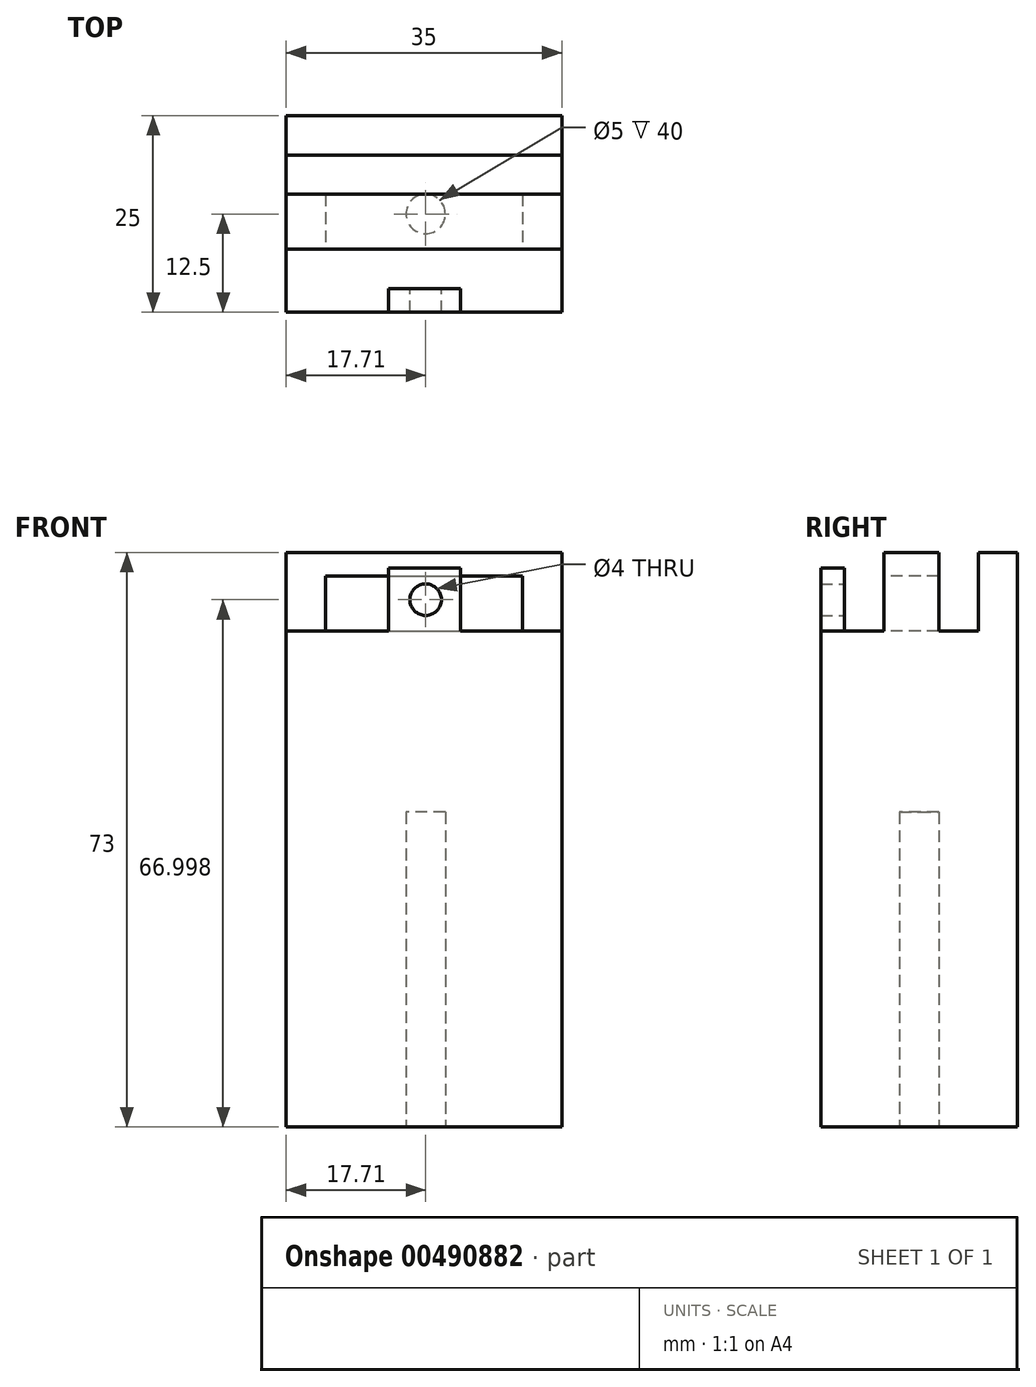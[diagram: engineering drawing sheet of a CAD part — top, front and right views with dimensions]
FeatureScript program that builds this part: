
annotation { "Feature Type Name" : "Feature", "Feature Type Description" : "" }
export const myFeature = defineFeature(function(context is Context, id is Id, definition is map)
    precondition{}
    {
        {
            var Q0;
            Q0=qCreatedBy(makeId("Top.planeOp"),FACE);
            var sketch = newSketch(context, id + "F0", { "sketchPlane" : qUnion([Q0])});
            skLineSegment(sketch, "E0.bottom", {"start": v(-17.7, 12.5) * mm, "end": v(17.3, 12.5) * mm});
            skLineSegment(sketch, "E0.top", {"start": v(-17.7, -12.5) * mm, "end": v(17.3, -12.5) * mm});
            skLineSegment(sketch, "E0.left", {"start": v(-17.7, 12.5) * mm, "end": v(-17.7, -12.5) * mm});
            skLineSegment(sketch, "E0.right", {"start": v(17.3, 12.5) * mm, "end": v(17.3, -12.5) * mm});
            skCircle(sketch, "E1", {"center": v(0, 0) * mm, "radius": 2.5 * mm});
            skSolve(sketch);
        }
        {
            var Q0;
            Q0 = qSketchRegion(id + "F0", true);
            extrude(context, id + "F1", {"entities" : qUnion([Q0]), "depth" : 40 * mm});
        }
        {
            var Q0;
            Q0=makeQuery(id+"F1.opExtrude","CAP_FACE",FACE,{"disambiguationData":[OSD([sQuery(id+"F0.wireOp",EDGE,"E0.bottom"),sQuery(id+"F0.wireOp",EDGE,"E0.top"),sQuery(id+"F0.wireOp",EDGE,"E0.left"),sQuery(id+"F0.wireOp",EDGE,"E0.right"),sQuery(id+"F0.wireOp",EDGE,"E1")])],"isStart":false});
            var sketch = newSketch(context, id + "F2", { "sketchPlane" : qUnion([Q0])});
            skLineSegment(sketch, "E2.bottom", {"start": v(-17.7, 12.5) * mm, "end": v(17.3, 12.5) * mm});
            skLineSegment(sketch, "E2.top", {"start": v(-17.7, -12.5) * mm, "end": v(17.3, -12.5) * mm});
            skLineSegment(sketch, "E2.left", {"start": v(-17.7, 12.5) * mm, "end": v(-17.7, -12.5) * mm});
            skLineSegment(sketch, "E2.right", {"start": v(17.3, 12.5) * mm, "end": v(17.3, -12.5) * mm});
            skSolve(sketch);
        }
        {
            var Q0;
            Q0 = qSketchRegion(id + "F2", true);
            extrude(context, id + "F3", {"entities" : qUnion([Q0]), "operationType" : NewBodyOperationType.ADD, "depth" : 23 * mm});
        }
        {
            var Q0;
            Q0=makeQuery(id+"F3.opExtrude","CAP_FACE",FACE,{"disambiguationData":[OSD([sQuery(id+"F2.wireOp",EDGE,"E2.bottom"),sQuery(id+"F2.wireOp",EDGE,"E2.top"),sQuery(id+"F2.wireOp",EDGE,"E2.left"),sQuery(id+"F2.wireOp",EDGE,"E2.right")])],"isStart":false});
            var sketch = newSketch(context, id + "F4", { "sketchPlane" : qUnion([Q0])});
            skLineSegment(sketch, "E3.bottom", {"start": v(-17.7, 12.5) * mm, "end": v(17.3, 12.5) * mm});
            skLineSegment(sketch, "E3.top", {"start": v(-17.7, 7.5) * mm, "end": v(17.3, 7.5) * mm});
            skLineSegment(sketch, "E3.left", {"start": v(-17.7, 12.5) * mm, "end": v(-17.7, 7.5) * mm});
            skLineSegment(sketch, "E3.right", {"start": v(17.3, 12.5) * mm, "end": v(17.3, 7.5) * mm});
            skSolve(sketch);
        }
        {
            var Q0;
            Q0 = qSketchRegion(id + "F4", true);
            extrude(context, id + "F5", {"entities" : qUnion([Q0]), "operationType" : NewBodyOperationType.ADD, "depth" : 10 * mm});
        }
        {
            var Q0;
            Q0=makeQuery(id+"F3.opExtrude","CAP_FACE",FACE,{"disambiguationData":[OSD([sQuery(id+"F2.wireOp",EDGE,"E2.bottom"),sQuery(id+"F2.wireOp",EDGE,"E2.top"),sQuery(id+"F2.wireOp",EDGE,"E2.left"),sQuery(id+"F2.wireOp",EDGE,"E2.right")])],"isStart":false});
            var sketch = newSketch(context, id + "F6", { "sketchPlane" : qUnion([Q0])});
            skLineSegment(sketch, "E4.bottom", {"start": v(-17.7, 2.5) * mm, "end": v(17.3, 2.5) * mm});
            skLineSegment(sketch, "E4.top", {"start": v(-17.7, -4.5) * mm, "end": v(17.3, -4.5) * mm});
            skLineSegment(sketch, "E4.left", {"start": v(-17.7, 2.5) * mm, "end": v(-17.7, -4.5) * mm});
            skLineSegment(sketch, "E4.right", {"start": v(17.3, 2.5) * mm, "end": v(17.3, -4.5) * mm});
            skSolve(sketch);
        }
        {
            var Q0;
            Q0 = qSketchRegion(id + "F6", true);
            extrude(context, id + "F7", {"entities" : qUnion([Q0]), "operationType" : NewBodyOperationType.ADD, "depth" : 10 * mm});
        }
        {
            var Q0;
            Q0=makeQuery(id+"F7.opExtrude","SWEPT_FACE",FACE,{"disambiguationData":[OSD([sQuery(id+"F6.wireOp",EDGE,"E4.top")])]});
            var sketch = newSketch(context, id + "F8", { "sketchPlane" : qUnion([Q0])});
            skLineSegment(sketch, "E5.bottom", {"start": v(-12.7, 70) * mm, "end": v(12.3, 70) * mm});
            skLineSegment(sketch, "E5.top", {"start": v(-12.7, 63) * mm, "end": v(12.3, 63) * mm});
            skLineSegment(sketch, "E5.left", {"start": v(-12.7, 70) * mm, "end": v(-12.7, 63) * mm});
            skLineSegment(sketch, "E5.right", {"start": v(12.3, 70) * mm, "end": v(12.3, 63) * mm});
            skSolve(sketch);
        }
        {
            var Q0;
            Q0 = qSketchRegion(id + "F8", true);
            extrude(context, id + "F9", {"entities" : qUnion([Q0]), "operationType" : NewBodyOperationType.REMOVE, "oppositeDirection" : true, "depth" : 7 * mm});
        }
        {
            var Q0;
            {var subQ1=sQuery(id+"F2.wireOp",EDGE,"E2.right");var subQ3=sQuery(id+"F2.wireOp",EDGE,"E2.left");var subQ8=sQuery(id+"F2.wireOp",EDGE,"E2.top");var subQ9=makeQuery(id+"F3.opExtrude","CAP_FACE",FACE,{"disambiguationData":[OSD([sQuery(id+"F2.wireOp",EDGE,"E2.bottom"),subQ8,subQ3,subQ1])],"isStart":false});Q0=makeQuery(id+"F9.boolean.opBoolean","MERGE",FACE,{"derivedFrom":[makeQuery(id+"F7.boolean.opBoolean","SPLIT",FACE,{"disambiguationData":[TD([makeQuery(id+"F1.opExtrude","SWEPT_FACE",FACE,{"disambiguationData":[OSD([sQuery(id+"F0.wireOp",EDGE,"E0.top")])]})])],"derivedFrom":subQ9}),makeQuery(id+"F7.boolean.opBoolean","SPLIT",FACE,{"disambiguationData":[TD([makeQuery(id+"F5.opExtrude","SWEPT_FACE",FACE,{"disambiguationData":[OSD([sQuery(id+"F4.wireOp",EDGE,"E3.top")])]})])],"derivedFrom":subQ9}),makeQuery(id+"F9.opExtrude","SWEPT_FACE",FACE,{"disambiguationData":[OSD([sQuery(id+"F8.wireOp",EDGE,"E5.top")])]})]});}
            var sketch = newSketch(context, id + "F10", { "sketchPlane" : qUnion([Q0])});
            skLineSegment(sketch, "E6.bottom", {"start": v(-4.7, -9.5) * mm, "end": v(4.46, -9.5) * mm});
            skLineSegment(sketch, "E6.top", {"start": v(-4.7, -12.5) * mm, "end": v(4.46, -12.5) * mm});
            skLineSegment(sketch, "E6.left", {"start": v(-4.7, -9.5) * mm, "end": v(-4.7, -12.5) * mm});
            skLineSegment(sketch, "E6.right", {"start": v(4.46, -9.5) * mm, "end": v(4.46, -12.5) * mm});
            skSolve(sketch);
        }
        {
            var Q0;
            Q0=makeQuery(id+"F10.imprint","IMPRINT",FACE,{"disambiguationData":[TD([[makeQuery(id+"F10.imprint","IMPRINT",EDGE,{"derivedFrom":sQuery(id+"F10.wireOp",EDGE,"E6.bottom")}),-1.0]])]});
            extrude(context, id + "F11", {"entities" : qUnion([Q0]), "operationType" : NewBodyOperationType.ADD, "depth" : 8 * mm});
        }
        {
            var Q0;
            Q0=makeQuery(id+"F11.boolean.opBoolean","MERGE",FACE,{"derivedFrom":[makeQuery(id+"F3.boolean.opBoolean","MERGE",FACE,{"derivedFrom":[makeQuery(id+"F1.opExtrude","SWEPT_FACE",FACE,{"disambiguationData":[OSD([sQuery(id+"F0.wireOp",EDGE,"E0.top")])]}),makeQuery(id+"F3.opExtrude","SWEPT_FACE",FACE,{"disambiguationData":[OSD([sQuery(id+"F2.wireOp",EDGE,"E2.top")])]})]}),makeQuery(id+"F11.opExtrude","SWEPT_FACE",FACE,{"disambiguationData":[OSD([sQuery(id+"F10.wireOp",EDGE,"E6.top")])]})]});
            var sketch = newSketch(context, id + "F12", { "sketchPlane" : qUnion([Q0])});
            skLineSegment(sketch, "E7.bottom", {"start": v(-4.7, 71) * mm, "end": v(4.46, 71) * mm});
            skLineSegment(sketch, "E7.top", {"start": v(-4.7, 63) * mm, "end": v(4.46, 63) * mm});
            skLineSegment(sketch, "E7.left", {"start": v(-4.7, 71) * mm, "end": v(-4.7, 63) * mm});
            skLineSegment(sketch, "E7.right", {"start": v(4.46, 71) * mm, "end": v(4.46, 63) * mm});
            skCircle(sketch, "E8", {"center": v(0, 67) * mm, "radius": 2 * mm});
            skPoint(sketch, "E8.centerSnap0", {"position": v(-4.7, 67) * mm});
            skSolve(sketch);
        }
        {
            var Q0;
            Q0=makeQuery(id+"F11.opExtrude","SWEPT_FACE",FACE,{"disambiguationData":[OSD([sQuery(id+"F10.wireOp",EDGE,"E6.bottom")])]});
            var sketch = newSketch(context, id + "F13", { "sketchPlane" : qUnion([Q0])});
            skCircle(sketch, "E9", {"center": v(0, 67) * mm, "radius": 2 * mm});
            skSolve(sketch);
        }
        {
            var Q0;
            Q0=sQuery(id+"F13.wireOp",VERTEX,"E9.center");
            var Q1;
            Q1=makeQuery(id+"F1.opExtrude","SWEPT_BODY",BODY,{"disambiguationData":[OSD([sQuery(id+"F0.wireOp",EDGE,"E0.bottom"),sQuery(id+"F0.wireOp",EDGE,"E0.top"),sQuery(id+"F0.wireOp",EDGE,"E0.left"),sQuery(id+"F0.wireOp",EDGE,"E0.right"),sQuery(id+"F0.wireOp",EDGE,"E1")])]});
            hole(context, id + "F14", {"style" : HoleStyle.SIMPLE, "endStyle" : HoleEndStyle.THROUGH, "holeDiameter" : 4 * mm, "isTappedThrough" : true, "tappedDepth" : 12 * mm, "tapClearance" : 3, "locations" : qUnion([Q0]), "scope" : qUnion([Q1])});
        }
    });
